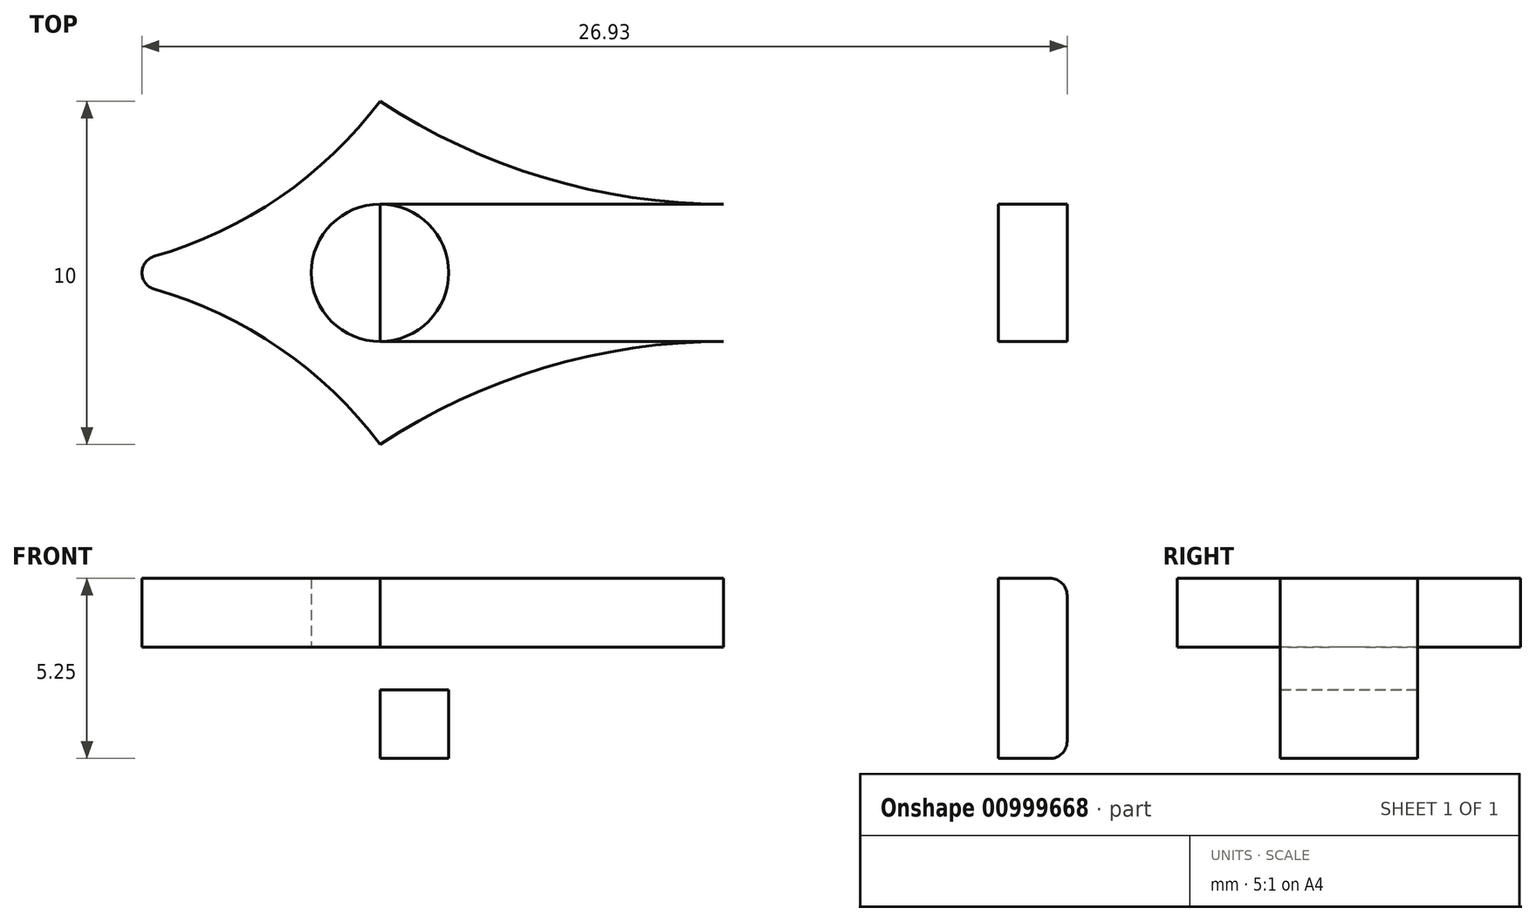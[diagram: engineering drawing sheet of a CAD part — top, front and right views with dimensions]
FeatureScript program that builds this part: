
annotation { "Feature Type Name" : "Feature", "Feature Type Description" : "" }
export const myFeature = defineFeature(function(context is Context, id is Id, definition is map)
    precondition{}
    {
        {
            assignVariable(context, id + "F0", {"name" : "h", "anyValue" : 4});
        }
        {
            assignVariable(context, id + "F1", {"name" : "t", "anyValue" : 2});
        }
        {
            assignVariable(context, id + "F2", {"name" : "ct", "anyValue" : 1.25});
        }
        {
            var Q0;
            Q0=qCreatedBy(makeId("Top.planeOp"),FACE);
            var sketch = newSketch(context, id + "F3", { "sketchPlane" : qUnion([Q0])});
            skLineSegment(sketch, "E0", {"start": v(0, 0) * mm, "end": v(0, 2) * mm});
            skLineSegment(sketch, "E1", {"start": v(0, 0) * mm, "end": v(-18, 0) * mm, "construction": true});
            skCircle(sketch, "E2", {"center": v(-18, 0) * mm, "radius": 2 * mm});
            skLineSegment(sketch, "E3", {"start": v(-18, 0) * mm, "end": v(-28, 0) * mm, "construction": true});
            skLineSegment(sketch, "E4", {"start": v(-18, 5) * mm, "end": v(-18, -5) * mm, "construction": true});
            skPoint(sketch, "E5", {"position": v(-8, 0) * mm});
            skLineSegment(sketch, "E6", {"start": v(0, 2) * mm, "end": v(-8, 2) * mm});
            skArc(sketch, "E7", {"start": v(-18, 5) * mm, "mid": v(-13.22, 2.77) * mm, "end": v(-8, 2) * mm});
            skArc(sketch, "E8", {"start": v(-24.57, 0.48) * mm, "mid": v(-20.91, 2.2) * mm, "end": v(-18, 5) * mm});
            skLineSegment(sketch, "E9.MirrorCS", {"start": v(0, -2) * mm, "end": v(-8, -2) * mm});
            skLineSegment(sketch, "E10.MirrorCS", {"start": v(0, 0) * mm, "end": v(0, -2) * mm});
            skArc(sketch, "E11.MirrorCS", {"start": v(-24.57, -0.48) * mm, "mid": v(-20.91, -2.2) * mm, "end": v(-18, -5) * mm});
            skArc(sketch, "E12.MirrorCS", {"start": v(-18, -5) * mm, "mid": v(-13.22, -2.77) * mm, "end": v(-8, -2) * mm});
            skLineSegment(sketch, "E13.bottom", {"start": v(0, 2) * mm, "end": v(-18, 2) * mm});
            skLineSegment(sketch, "E13.top", {"start": v(0, -2) * mm, "end": v(-18, -2) * mm});
            skLineSegment(sketch, "E13.left", {"start": v(0, 2) * mm, "end": v(0, -2) * mm});
            skLineSegment(sketch, "E13.right", {"start": v(-18, 2) * mm, "end": v(-18, -2) * mm});
            skLineSegment(sketch, "E14.bottom", {"start": v(0, 2) * mm, "end": v(2, 2) * mm});
            skLineSegment(sketch, "E14.top", {"start": v(0, -2) * mm, "end": v(2, -2) * mm});
            skLineSegment(sketch, "E14.right", {"start": v(2, 2) * mm, "end": v(2, -2) * mm});
            skPoint(sketch, "E15.visualSharp", {"position": v(-28, 0) * mm});
            skArc(sketch, "E15.filletArc", {"start": v(-24.57, 0.48) * mm, "mid": v(-24.93, 0) * mm, "end": v(-24.57, -0.48) * mm});
            skSolve(sketch);
        }
        {
            var Q0;
            {var subQ0=sQuery(id+"F3.wireOp",EDGE,"E7");Q0=makeQuery(id+"F3.imprint","IMPRINT",FACE,{"disambiguationData":[TD([[makeQuery(id+"F3.imprint","IMPRINT",EDGE,{"derivedFrom":subQ0}),-1.0]])]});}
            var Q1;
            {var subQ2=sQuery(id+"F3.wireOp",EDGE,"E13.left");Q1=makeQuery(id+"F3.imprint","IMPRINT",FACE,{"disambiguationData":[TD([[makeQuery(id+"F3.imprint","IMPRINT",EDGE,{"derivedFrom":subQ2}),-1.0]])]});}
            var Q2;
            {var subQ2=sQuery(id+"F3.wireOp",EDGE,"E13.left");Q2=makeQuery(id+"F3.imprint","IMPRINT",FACE,{"disambiguationData":[TD([[makeQuery(id+"F3.imprint","IMPRINT",EDGE,{"derivedFrom":subQ2}),-1.0]])]});}
            var Q3;
            Q3=makeQuery(id+"F3.imprint","IMPRINT",FACE,{"disambiguationData":[TD([[makeQuery(id+"F3.imprint","IMPRINT",EDGE,{"derivedFrom":sQuery(id+"F3.wireOp",EDGE,"E14.bottom")}),-1.0]])]});
            extrude(context, id + "F4", {"entities" : qUnion([Q0, Q1, Q2, Q3]), "depth" : getVariable(context, 't') * mm, "offsetDistance" : 25 * mm});
        }
        {
            var Q0;
            Q0=makeQuery(id+"F3.imprint","IMPRINT",FACE,{"disambiguationData":[TD([[makeQuery(id+"F3.imprint","IMPRINT",EDGE,{"derivedFrom":sQuery(id+"F3.wireOp",EDGE,"E14.bottom")}),-1.0]])]});
            extrude(context, id + "F5", {"entities" : qUnion([Q0]), "operationType" : NewBodyOperationType.ADD, "oppositeDirection" : true, "depth" : (getVariable(context, 'ct')) * mm, "offsetDistance" : 25 * mm});
        }
        {
            var Q0;
            {var subQ0=sQuery(id+"F3.wireOp",EDGE,"E13.right");Q0=makeQuery(id+"F3.imprint","IMPRINT",FACE,{"disambiguationData":[TD([[makeQuery(id+"F3.imprint","IMPRINT",EDGE,{"derivedFrom":subQ0}),1.0]])]});}
            var Q1;
            {var subQ2=sQuery(id+"F3.wireOp",EDGE,"E13.left");Q1=makeQuery(id+"F3.imprint","IMPRINT",FACE,{"disambiguationData":[TD([[makeQuery(id+"F3.imprint","IMPRINT",EDGE,{"derivedFrom":subQ2}),-1.0]])]});}
            var Q2;
            Q2=makeQuery(id+"F3.imprint","IMPRINT",FACE,{"disambiguationData":[TD([[makeQuery(id+"F3.imprint","IMPRINT",EDGE,{"derivedFrom":sQuery(id+"F3.wireOp",EDGE,"E14.bottom")}),-1.0]])]});
            extrude(context, id + "F6", {"entities" : qUnion([Q0, Q1, Q2]), "operationType" : NewBodyOperationType.ADD, "oppositeDirection" : true, "depth" : (getVariable(context, 'ct') + getVariable(context, 't')) * mm, "offsetDistance" : 25 * mm, "hasSecondDirection" : true, "secondDirectionOppositeDirection" : true, "secondDirectionDepth" : (getVariable(context, 'ct')) * mm});
        }
        {
            var Q0;
            {var subQ0=sQuery(id+"F3.wireOp",EDGE,"E14.top");var subQ1=sQuery(id+"F3.wireOp",EDGE,"E13.top");Q0=makeQuery(id+"F6.boolean.opBoolean","MERGE",FACE,{"derivedFrom":[makeQuery(id+"F5.boolean.opBoolean","MERGE",FACE,{"derivedFrom":[makeQuery(id+"F4.opExtrude","SWEPT_FACE",FACE,{"disambiguationData":[OSD([subQ1,subQ0])]}),makeQuery(id+"F5.opExtrude","SWEPT_FACE",FACE,{"disambiguationData":[OSD([subQ0])]})]}),makeQuery(id+"F6.opExtrude","SWEPT_FACE",FACE,{"disambiguationData":[OSD([subQ1,subQ0])]})]});}
            var sketch = newSketch(context, id + "F7", { "sketchPlane" : qUnion([Q0])});
            skLineSegment(sketch, "E16.bottom", {"start": v(-18, -3.25) * mm, "end": v(-13.63, -3.25) * mm});
            skLineSegment(sketch, "E16.top", {"start": v(-17.5, -1.25) * mm, "end": v(-13.63, -1.25) * mm});
            skLineSegment(sketch, "E16.left", {"start": v(-18, -3.25) * mm, "end": v(-18, -1.75) * mm});
            skLineSegment(sketch, "E16.right", {"start": v(-13.63, -3.25) * mm, "end": v(-13.63, -1.25) * mm});
            skLineSegment(sketch, "E17.bottom", {"start": v(1.5, 2) * mm, "end": v(0, 2) * mm});
            skLineSegment(sketch, "E17.top", {"start": v(1.5, -3.25) * mm, "end": v(0, -3.25) * mm});
            skLineSegment(sketch, "E17.left", {"start": v(2, 1.5) * mm, "end": v(2, -2.75) * mm});
            skLineSegment(sketch, "E17.right", {"start": v(0, 2) * mm, "end": v(0, -3.25) * mm});
            skPoint(sketch, "E18.visualSharp", {"position": v(-18, -1.25) * mm});
            skArc(sketch, "E18.filletArc", {"start": v(-17.5, -1.25) * mm, "mid": v(-17.85, -1.4) * mm, "end": v(-18, -1.75) * mm});
            skPoint(sketch, "E19.visualSharp", {"position": v(2, 2) * mm});
            skArc(sketch, "E19.filletArc", {"start": v(2, 1.5) * mm, "mid": v(1.85, 1.85) * mm, "end": v(1.5, 2) * mm});
            skPoint(sketch, "E20.visualSharp", {"position": v(2, -3.25) * mm});
            skArc(sketch, "E20.filletArc", {"start": v(1.5, -3.25) * mm, "mid": v(1.85, -3.1) * mm, "end": v(2, -2.75) * mm});
            skSolve(sketch);
        }
        {
            var Q0;
            {var subQ0=sQuery(id+"F7.wireOp",EDGE,"4a116d95-578f-45bf-83a4-0684aafd2bff.filletArc");Q0=makeQuery(id+"F7.imprint","IMPRINT",FACE,{"disambiguationData":[TD([[makeQuery(id+"F7.imprint","IMPRINT",EDGE,{"derivedFrom":subQ0}),-1.0]])]});}
            var Q1;
            {var subQ0=sQuery(id+"F7.wireOp",EDGE,"E18.filletArc");Q1=makeQuery(id+"F7.imprint","IMPRINT",FACE,{"disambiguationData":[TD([[makeQuery(id+"F7.imprint","IMPRINT",EDGE,{"derivedFrom":subQ0}),-1.0]])]});}
            var Q2;
            {var subQ0=sQuery(id+"F7.wireOp",EDGE,"E19.filletArc");Q2=makeQuery(id+"F7.imprint","IMPRINT",FACE,{"disambiguationData":[TD([[makeQuery(id+"F7.imprint","IMPRINT",EDGE,{"derivedFrom":subQ0}),-1.0]])]});}
            var Q3;
            {var subQ0=sQuery(id+"F7.wireOp",EDGE,"E20.filletArc");Q3=makeQuery(id+"F7.imprint","IMPRINT",FACE,{"disambiguationData":[TD([[makeQuery(id+"F7.imprint","IMPRINT",EDGE,{"derivedFrom":subQ0}),-1.0]])]});}
            extrude(context, id + "F8", {"entities" : qUnion([Q0, Q1, Q2, Q3]), "operationType" : NewBodyOperationType.REMOVE, "oppositeDirection" : true, "depth" : (getVariable(context, 'h')) * mm, "offsetDistance" : 25 * mm});
        }
    });
